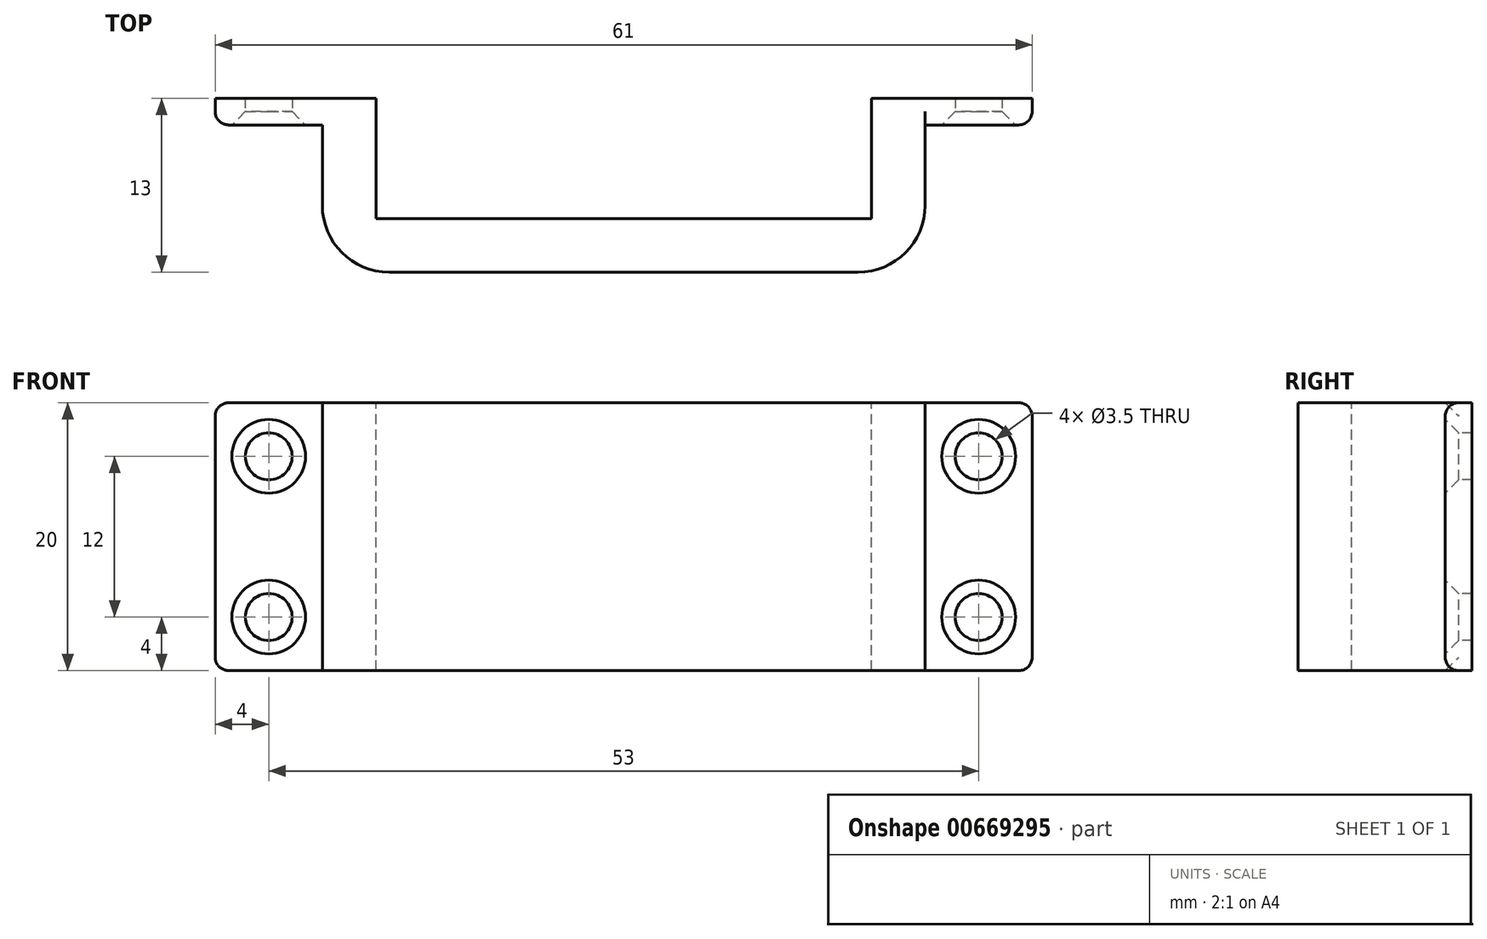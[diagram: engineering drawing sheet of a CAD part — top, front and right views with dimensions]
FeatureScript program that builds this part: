
annotation { "Feature Type Name" : "Feature", "Feature Type Description" : "" }
export const myFeature = defineFeature(function(context is Context, id is Id, definition is map)
    precondition{}
    {
        {
            var Q0;
            Q0=qCreatedBy(makeId("Front.planeOp"),FACE);
            var sketch = newSketch(context, id + "F0", { "sketchPlane" : qUnion([Q0])});
            skLineSegment(sketch, "E0.bottom", {"start": v(18.5, -10) * mm, "end": v(-18.5, -10) * mm});
            skLineSegment(sketch, "E0.top", {"start": v(18.5, 10) * mm, "end": v(-18.5, 10) * mm});
            skLineSegment(sketch, "E0.left", {"start": v(18.5, -10) * mm, "end": v(18.5, 10) * mm});
            skLineSegment(sketch, "E0.right", {"start": v(-18.5, -10) * mm, "end": v(-18.5, 10) * mm});
            skPoint(sketch, "E0.middle", {"position": v(0, 0) * mm});
            skLineSegment(sketch, "E1", {"start": v(18.5, 10) * mm, "end": v(22.5, 10) * mm});
            skLineSegment(sketch, "E2", {"start": v(22.5, 10) * mm, "end": v(22.5, -10) * mm});
            skLineSegment(sketch, "E3", {"start": v(22.5, -10) * mm, "end": v(18.5, -10) * mm});
            skLineSegment(sketch, "E4", {"start": v(-18.5, 10) * mm, "end": v(-22.5, 10) * mm});
            skLineSegment(sketch, "E5", {"start": v(-22.5, 10) * mm, "end": v(-22.5, -10) * mm});
            skLineSegment(sketch, "E6", {"start": v(-22.5, -10) * mm, "end": v(-18.5, -10) * mm});
            skSolve(sketch);
        }
        {
            var Q0;
            Q0=makeQuery(id+"F0.imprint","IMPRINT",FACE,{"disambiguationData":[TD([[makeQuery(id+"F0.imprint","IMPRINT",EDGE,{"derivedFrom":sQuery(id+"F0.wireOp",EDGE,"E0.right")}),1.0]])]});
            var Q1;
            Q1=makeQuery(id+"F0.imprint","IMPRINT",FACE,{"disambiguationData":[TD([[makeQuery(id+"F0.imprint","IMPRINT",EDGE,{"derivedFrom":sQuery(id+"F0.wireOp",EDGE,"E0.bottom")}),-1.0]])]});
            var Q2;
            Q2=makeQuery(id+"F0.imprint","IMPRINT",FACE,{"disambiguationData":[TD([[makeQuery(id+"F0.imprint","IMPRINT",EDGE,{"derivedFrom":sQuery(id+"F0.wireOp",EDGE,"E0.left")}),-1.0]])]});
            extrude(context, id + "F1", {"entities" : qUnion([Q0, Q1, Q2]), "depth" : 4 * mm, "offsetDistance" : 25 * mm});
        }
        {
            var Q0;
            Q0=makeQuery(id+"F0.imprint","IMPRINT",FACE,{"disambiguationData":[TD([[makeQuery(id+"F0.imprint","IMPRINT",EDGE,{"derivedFrom":sQuery(id+"F0.wireOp",EDGE,"E0.right")}),1.0]])]});
            var Q1;
            Q1=makeQuery(id+"F0.imprint","IMPRINT",FACE,{"disambiguationData":[TD([[makeQuery(id+"F0.imprint","IMPRINT",EDGE,{"derivedFrom":sQuery(id+"F0.wireOp",EDGE,"E0.left")}),-1.0]])]});
            extrude(context, id + "F2", {"entities" : qUnion([Q0, Q1]), "operationType" : NewBodyOperationType.ADD, "oppositeDirection" : true, "depth" : 9 * mm, "offsetDistance" : 25 * mm});
        }
        {
            var Q0;
            Q0=makeQuery(id+"F2.opExtrude","CAP_FACE",FACE,{"disambiguationData":[OSD([sQuery(id+"F0.wireOp",EDGE,"E0.left"),sQuery(id+"F0.wireOp",EDGE,"E1"),sQuery(id+"F0.wireOp",EDGE,"E2"),sQuery(id+"F0.wireOp",EDGE,"E3")])],"isStart":false});
            var sketch = newSketch(context, id + "F3", { "sketchPlane" : qUnion([Q0])});
            skLineSegment(sketch, "E7.bottom", {"start": v(-22.5, 10) * mm, "end": v(-30.5, 10) * mm});
            skLineSegment(sketch, "E7.top", {"start": v(-22.5, -10) * mm, "end": v(-30.5, -10) * mm});
            skLineSegment(sketch, "E7.left", {"start": v(-22.5, 10) * mm, "end": v(-22.5, -10) * mm});
            skLineSegment(sketch, "E7.right", {"start": v(-30.5, 10) * mm, "end": v(-30.5, -10) * mm});
            skLineSegment(sketch, "E8.0", {"start": v(22.5, 10) * mm, "end": v(22.5, -10) * mm});
            skLineSegment(sketch, "E9", {"start": v(22.5, 10) * mm, "end": v(30.5, 10) * mm});
            skLineSegment(sketch, "E10", {"start": v(30.5, 10) * mm, "end": v(30.5, -10) * mm});
            skLineSegment(sketch, "E11", {"start": v(30.5, -10) * mm, "end": v(22.5, -10) * mm});
            skSolve(sketch);
        }
        {
            var Q0;
            Q0=makeQuery(id+"F3.imprint","IMPRINT",FACE,{"disambiguationData":[TD([[makeQuery(id+"F3.imprint","IMPRINT",EDGE,{"derivedFrom":sQuery(id+"F3.wireOp",EDGE,"E7.bottom")}),1.0]])]});
            var Q1;
            Q1=makeQuery(id+"F3.imprint","IMPRINT",FACE,{"disambiguationData":[TD([[makeQuery(id+"F3.imprint","IMPRINT",EDGE,{"derivedFrom":sQuery(id+"F3.wireOp",EDGE,"E8.0")}),1.0]])]});
            extrude(context, id + "F4", {"entities" : qUnion([Q0, Q1]), "operationType" : NewBodyOperationType.ADD, "oppositeDirection" : true, "depth" : 2 * mm, "offsetDistance" : 25 * mm});
        }
        {
            var Q0;
            Q0=makeQuery(id+"F4.opExtrude","CAP_FACE",FACE,{"disambiguationData":[OSD([sQuery(id+"F3.wireOp",EDGE,"E7.bottom"),sQuery(id+"F3.wireOp",EDGE,"E7.top"),sQuery(id+"F3.wireOp",EDGE,"E7.left"),sQuery(id+"F3.wireOp",EDGE,"E7.right")])],"isStart":false});
            var sketch = newSketch(context, id + "F5", { "sketchPlane" : qUnion([Q0])});
            skLineSegment(sketch, "E12", {"start": v(26.5, 10) * mm, "end": v(26.5, 6) * mm, "construction": true});
            skLineSegment(sketch, "E13", {"start": v(26.5, 6) * mm, "end": v(30.5, 6) * mm, "construction": true});
            skCircle(sketch, "E14", {"center": v(26.5, 6) * mm, "radius": 1.75 * mm});
            skLineSegment(sketch, "E15.0.0", {"start": v(-30.5, -10) * mm, "end": v(-22.5, -10) * mm});
            skLineSegment(sketch, "E15.0.1", {"start": v(-22.5, -10) * mm, "end": v(-22.5, 10) * mm});
            skLineSegment(sketch, "E15.0.2", {"start": v(-22.5, 10) * mm, "end": v(-30.5, 10) * mm});
            skLineSegment(sketch, "E15.0.3", {"start": v(-30.5, 10) * mm, "end": v(-30.5, -10) * mm});
            skLineSegment(sketch, "E16", {"start": v(-26.5, 10) * mm, "end": v(-26.5, 6) * mm, "construction": true});
            skLineSegment(sketch, "E17", {"start": v(-26.5, 6) * mm, "end": v(-30.5, 6) * mm, "construction": true});
            skCircle(sketch, "E18", {"center": v(-26.5, 6) * mm, "radius": 1.75 * mm});
            skLineSegment(sketch, "E19", {"start": v(-30.5, 0) * mm, "end": v(-22.5, 0) * mm, "construction": true});
            skLineSegment(sketch, "E20", {"start": v(-22.5, 0) * mm, "end": v(30.5, 0) * mm, "construction": true});
            skCircle(sketch, "E21.MirrorC", {"center": v(26.5, -6) * mm, "radius": 1.75 * mm});
            skCircle(sketch, "E22.MirrorC", {"center": v(-26.5, -6) * mm, "radius": 1.75 * mm});
            skSolve(sketch);
        }
        {
            var Q0;
            Q0=sQuery(id+"F5.wireOp",VERTEX,"E22.MirrorC.center");
            var Q1;
            Q1=sQuery(id+"F5.wireOp",VERTEX,"E18.center");
            var Q2;
            Q2=sQuery(id+"F5.wireOp",VERTEX,"E21.MirrorC.center");
            var Q3;
            Q3=sQuery(id+"F5.wireOp",VERTEX,"E14.center");
            var Q4;
            Q4=makeQuery(id+"F1.opExtrude","SWEPT_BODY",BODY,{"disambiguationData":[OSD([sQuery(id+"F0.wireOp",EDGE,"E0.bottom"),sQuery(id+"F0.wireOp",EDGE,"E0.top"),sQuery(id+"F0.wireOp",EDGE,"E1"),sQuery(id+"F0.wireOp",EDGE,"E2"),sQuery(id+"F0.wireOp",EDGE,"E3"),sQuery(id+"F0.wireOp",EDGE,"E4"),sQuery(id+"F0.wireOp",EDGE,"E5"),sQuery(id+"F0.wireOp",EDGE,"E6")])]});
            hole(context, id + "F6", {"style" : HoleStyle.C_SINK, "endStyle" : HoleEndStyle.THROUGH, "holeDiameter" : 3.5 * mm, "cSinkDiameter" : 5.5 * mm, "cSinkAngle" : 90 * degree, "majorDiameter" : 5 * mm, "isTappedThrough" : true, "tappedDepth" : 12 * mm, "tapClearance" : 3, "locations" : qUnion([Q0, Q1, Q2, Q3]), "scope" : qUnion([Q4])});
        }
        {
            var Q0;
            Q0=makeQuery(id+"F1.opExtrude","CAP_EDGE",EDGE,{"disambiguationData":[OSD([sQuery(id+"F0.wireOp",EDGE,"E2")])],"isStart":false});
            var Q1;
            Q1=makeQuery(id+"F1.opExtrude","CAP_EDGE",EDGE,{"disambiguationData":[OSD([sQuery(id+"F0.wireOp",EDGE,"E5")])],"isStart":false});
            fillet(context, id + "F7", {"entities" : qUnion([Q0, Q1]), "radius" : 5 * mm, "tangentPropagation" : true, "allowEdgeOverflow" : false});
        }
        {
            var Q0;
            Q0=makeQuery(id+"F4.opExtrude","CAP_EDGE",EDGE,{"disambiguationData":[OSD([sQuery(id+"F3.wireOp",EDGE,"E7.left")])],"isStart":false});
            var Q1;
            Q1=makeQuery(id+"F4.opExtrude","CAP_EDGE",EDGE,{"disambiguationData":[OSD([sQuery(id+"F3.wireOp",EDGE,"E8.0")])],"isStart":false});
            var Q2;
            Q2=makeQuery(id+"F4.opExtrude","CAP_EDGE",EDGE,{"disambiguationData":[OSD([sQuery(id+"F3.wireOp",EDGE,"E7.bottom")])],"isStart":false});
            var Q3;
            Q3=makeQuery(id+"F4.opExtrude","CAP_EDGE",EDGE,{"disambiguationData":[OSD([sQuery(id+"F3.wireOp",EDGE,"E7.top")])],"isStart":false});
            var Q4;
            Q4=makeQuery(id+"F4.opExtrude","CAP_EDGE",EDGE,{"disambiguationData":[OSD([sQuery(id+"F3.wireOp",EDGE,"E7.right")])],"isStart":false});
            var Q5;
            Q5=makeQuery(id+"F4.opExtrude","CAP_EDGE",EDGE,{"disambiguationData":[OSD([sQuery(id+"F3.wireOp",EDGE,"E10")])],"isStart":false});
            var Q6;
            Q6=makeQuery(id+"F4.opExtrude","SWEPT_EDGE",EDGE,{"disambiguationData":[OSD([sQuery(id+"F3.wireOp",EDGE,"E7.bottom"),sQuery(id+"F3.wireOp",EDGE,"E7.right")])]});
            var Q7;
            Q7=makeQuery(id+"F4.opExtrude","SWEPT_EDGE",EDGE,{"disambiguationData":[OSD([sQuery(id+"F3.wireOp",EDGE,"E7.top"),sQuery(id+"F3.wireOp",EDGE,"E7.right")])]});
            var Q8;
            Q8=makeQuery(id+"F4.opExtrude","SWEPT_EDGE",EDGE,{"disambiguationData":[OSD([sQuery(id+"F3.wireOp",EDGE,"E9"),sQuery(id+"F3.wireOp",EDGE,"E10")])]});
            var Q9;
            Q9=makeQuery(id+"F4.opExtrude","SWEPT_EDGE",EDGE,{"disambiguationData":[OSD([sQuery(id+"F3.wireOp",EDGE,"E10"),sQuery(id+"F3.wireOp",EDGE,"E11")])]});
            fillet(context, id + "F8", {"entities" : qUnion([Q0, Q1, Q2, Q3, Q4, Q5, Q6, Q7, Q8, Q9]), "radius" : 1 * mm, "tangentPropagation" : true, "allowEdgeOverflow" : false});
        }
    });
